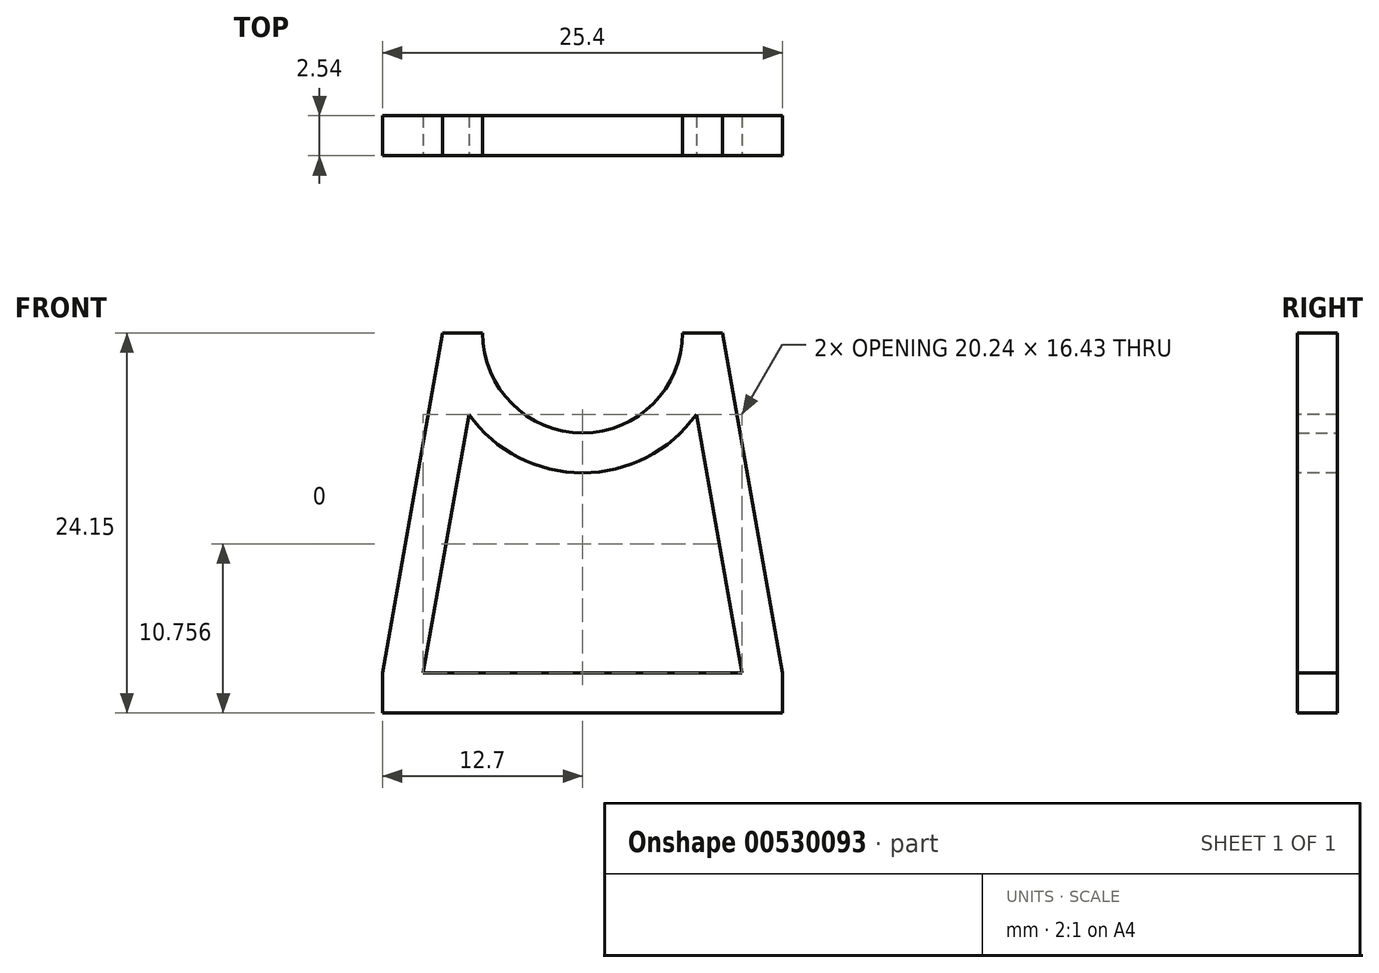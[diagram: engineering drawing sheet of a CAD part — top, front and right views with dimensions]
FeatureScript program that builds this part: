
annotation { "Feature Type Name" : "Feature", "Feature Type Description" : "" }
export const myFeature = defineFeature(function(context is Context, id is Id, definition is map)
    precondition{}
    {
        {
            var Q0;
            Q0=qCreatedBy(makeId("Front.planeOp"),FACE);
            var sketch = newSketch(context, id + "F0", { "sketchPlane" : qUnion([Q0])});
            skArc(sketch, "E0", {"start": v(-6.35, 0) * mm, "mid": v(0, -6.35) * mm, "end": v(6.35, 0) * mm});
            skLineSegment(sketch, "E1", {"start": v(-6.35, 0) * mm, "end": v(-8.9, 0) * mm});
            skLineSegment(sketch, "E2", {"start": v(6.35, 0) * mm, "end": v(8.9, 0) * mm});
            skLineSegment(sketch, "E3", {"start": v(8.9, 0) * mm, "end": v(12.7, -21.6) * mm});
            skLineSegment(sketch, "E4", {"start": v(12.7, -21.6) * mm, "end": v(12.7, -24.15) * mm});
            skLineSegment(sketch, "E5", {"start": v(12.7, -24.15) * mm, "end": v(-12.7, -24.15) * mm});
            skLineSegment(sketch, "E6", {"start": v(-12.7, -24.15) * mm, "end": v(-12.7, -21.6) * mm});
            skLineSegment(sketch, "E7", {"start": v(-12.7, -21.6) * mm, "end": v(-8.9, 0) * mm});
            skSolve(sketch);
        }
        {
            var Q0;
            Q0 = qSketchRegion(id + "F0", true);
            extrude(context, id + "F1", {"entities" : qUnion([Q0]), "depth" : 2.54 * mm, "offsetDistance" : 25.4 * mm});
        }
        {
            var Q0;
            Q0=makeQuery(id+"F1.opExtrude","SWEPT_BODY",BODY,{"disambiguationData":[OSD([sQuery(id+"F0.wireOp",EDGE,"E0"),sQuery(id+"F0.wireOp",EDGE,"E1"),sQuery(id+"F0.wireOp",EDGE,"E2"),sQuery(id+"F0.wireOp",EDGE,"E3"),sQuery(id+"F0.wireOp",EDGE,"E4"),sQuery(id+"F0.wireOp",EDGE,"E5"),sQuery(id+"F0.wireOp",EDGE,"E6"),sQuery(id+"F0.wireOp",EDGE,"E7")])]});
            transform(context, id + "F2", {"entities" : qUnion([Q0]), "transformType" : TransformType.TRANSLATION_3D, "dx" : 0 * mm, "dy" : 0 * mm, "dz" : 0 * mm, "makeCopy" : true});
        }
        {
            var Q0;
            Q0=makeQuery(id+"F2.opPattern","COPY",FACE,{"derivedFrom":makeQuery(id+"F1.opExtrude","CAP_FACE",FACE,{"disambiguationData":[OSD([sQuery(id+"F0.wireOp",EDGE,"E0"),sQuery(id+"F0.wireOp",EDGE,"E1"),sQuery(id+"F0.wireOp",EDGE,"E2"),sQuery(id+"F0.wireOp",EDGE,"E3"),sQuery(id+"F0.wireOp",EDGE,"E4"),sQuery(id+"F0.wireOp",EDGE,"E5"),sQuery(id+"F0.wireOp",EDGE,"E6"),sQuery(id+"F0.wireOp",EDGE,"E7")])],"isStart":false}),"instanceName":"1"});
            var sketch = newSketch(context, id + "F3", { "sketchPlane" : qUnion([Q0])});
            skLineSegment(sketch, "E8.0", {"start": v(-10.12, -21.6) * mm, "end": v(-7.22, -5.18) * mm});
            skLineSegment(sketch, "E8.1", {"start": v(10.12, -21.6) * mm, "end": v(-10.12, -21.6) * mm});
            skLineSegment(sketch, "E8.2", {"start": v(7.22, -5.18) * mm, "end": v(10.12, -21.6) * mm});
            skArc(sketch, "E8.3", {"start": v(-7.22, -5.18) * mm, "mid": v(0, -8.9) * mm, "end": v(7.22, -5.18) * mm});
            skSolve(sketch);
        }
        {
            var Q0;
            Q0=makeQuery(id+"F3.imprint","IMPRINT",FACE,{"disambiguationData":[TD([[makeQuery(id+"F3.imprint","IMPRINT",EDGE,{"derivedFrom":sQuery(id+"F3.wireOp",EDGE,"E8.0")}),-1.0]])]});
            extrude(context, id + "F4", {"entities" : qUnion([Q0]), "operationType" : NewBodyOperationType.REMOVE, "endBound" : BoundingType.THROUGH_ALL, "oppositeDirection" : true, "depth" : 25.4 * mm, "offsetDistance" : 25.4 * mm});
        }
    });
